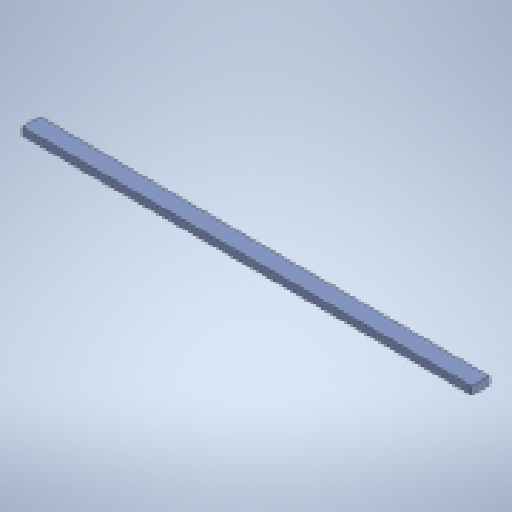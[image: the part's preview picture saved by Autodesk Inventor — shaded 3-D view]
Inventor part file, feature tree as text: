
AUTODESK INVENTOR PART (.ipt)
format: ipt  version: 2025.1 (Build 291241020, 241B)  size: 138,240 bytes
history: native  units: in
note: dims shown in document units (in); Inventor stores cm internally (conversion verified against a paired STEP export)
features: extrude x1, sketch x1, other x1
ambient origin geometry x8: Origin, YZ Plane, XZ Plane, XY Plane, X Axis, Y Axis, Z Axis, Center Point
bodies: Solid1 (feature_tree)
feature tree (3):
  extrude  "Extrusion1"  Depth=1.5in
  sketch  "Sketch1"  dims[d0=3.5in d1=1.5in d2=89.0in d3=0.0in]
  other  "Finish1"
